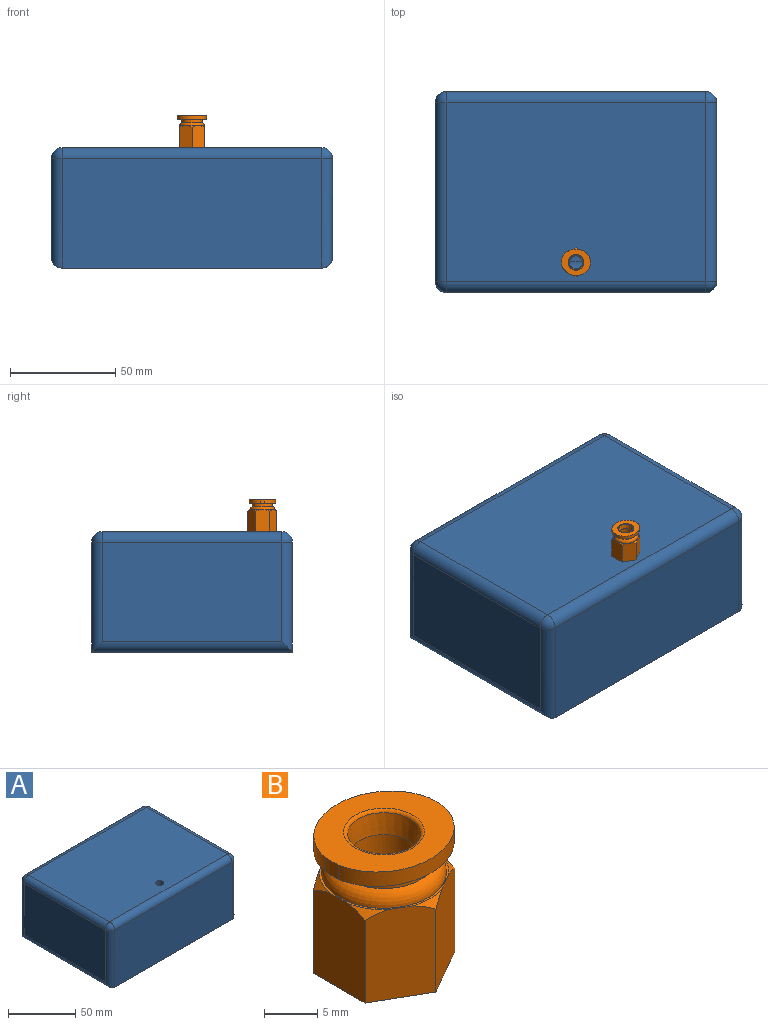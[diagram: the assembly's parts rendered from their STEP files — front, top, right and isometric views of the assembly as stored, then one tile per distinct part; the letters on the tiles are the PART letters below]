
ASSEMBLY  parts=2 mates=1
PART A: 47 faces, bbox 133.4x95.3x57.2 mm
  f0: plane 65.41x27.31mm, normal (-1,0,0), area 1785.9mm2, adj f18,f27,f28,f32
  f1: plane 103.51x27.31mm, normal (0,-1,0), area 2826.2mm2, adj f19,f20,f28,f29
  f2: plane 65.41x27.31mm, normal (1,0,0), area 1785.9mm2, adj f13,f16,f20,f21
  f3: plane 103.51x27.31mm, normal (0,1,0), area 2826.2mm2, adj f16,f17,f26,f27
  f4: plane 103.51x65.41mm, normal (0,0,-1), area 6758.9mm2, adj f6,f21,f26,f29,f32
  f5: plane 103.51x65.41mm, normal (0,0,1), area 6769.7mm2, adj f13,f17,f18,f19
  f6: cylinder r=3.11mm len=6.22mm, axis (0,0,1), area 97mm2, adj f4,f11,f26
  f7: plane 85.09x46.99mm, normal (1,0,0), area 3998.4mm2, adj f41,f43,f45,f46
  f8: plane 123.19x52.07mm, normal (0,1,0), area 6414.5mm2, adj f12,f37,f42,f46
  f9: plane 85.09x46.99mm, normal (-1,0,0), area 3998.4mm2, adj f33,f34,f36,f37
  f10: plane 123.19x52.07mm, normal (0,-1,0), area 6414.5mm2, adj f12,f33,f38,f43
  f11: plane 123.19x85.09mm, normal (0,0,1), area 10451.9mm2, adj f6,f36,f38,f41,f42
  f12: plane 123.19x95.25mm, normal (0,0,-1), area 11733.8mm2, adj f8,f10,f34,f45
  f13: cylinder r=10.16mm len=65.41mm, axis (0,1,0), area 1043.8mm2, adj f2,f5,f14,f15
  f14: sphere r=10.16mm, area 162.1mm2, adj f13,f16,f17
  f15: sphere r=10.16mm, area 162.1mm2, adj f13,f19,f20
  f16: cylinder r=10.16mm len=27.31mm, axis (0,0,1), area 435.8mm2, adj f2,f3,f14,f22
  f17: cylinder r=10.16mm len=103.51mm, axis (-1,0,0), area 1651.9mm2, adj f3,f5,f14,f23
  f18: cylinder r=10.16mm len=65.41mm, axis (0,-1,0), area 1043.8mm2, adj f0,f5,f23,f24
  f19: cylinder r=10.16mm len=103.51mm, axis (1,0,0), area 1651.9mm2, adj f1,f5,f15,f24
  f20: cylinder r=10.16mm len=27.31mm, axis (0,0,-1), area 435.8mm2, adj f1,f2,f15,f25
  f21: cylinder r=10.16mm len=65.41mm, axis (0,-1,0), area 1043.8mm2, adj f2,f4,f22,f25
  f22: sphere r=10.16mm, area 162.1mm2, adj f16,f21,f26
  f23: sphere r=10.16mm, area 162.1mm2, adj f17,f18,f27
  f24: sphere r=10.16mm, area 162.1mm2, adj f18,f19,f28
  f25: sphere r=10.16mm, area 162.1mm2, adj f20,f21,f29
  f26: cylinder r=10.16mm len=103.51mm, axis (1,0,0), area 1632mm2, adj f3,f4,f6,f22,f30
  f27: cylinder r=10.16mm len=27.31mm, axis (0,0,-1), area 435.8mm2, adj f0,f3,f23,f30
  f28: cylinder r=10.16mm len=27.31mm, axis (0,0,1), area 435.8mm2, adj f0,f1,f24,f31
  f29: cylinder r=10.16mm len=103.51mm, axis (-1,0,0), area 1651.9mm2, adj f1,f4,f25,f31
  f30: sphere r=10.16mm, area 162.1mm2, adj f26,f27,f32
  f31: sphere r=10.16mm, area 162.1mm2, adj f28,f29,f32
  f32: cylinder r=10.16mm len=65.41mm, axis (0,1,0), area 1043.8mm2, adj f0,f4,f30,f31
  f33: cylinder r=5.08mm len=52.07mm, axis (0,0,-1), area 400.8mm2, adj f9,f10,f34,f35
  f34: cylinder r=5.08mm len=95.25mm, axis (0,-1,0), area 730.6mm2, adj f9,f12,f33,f37
  f35: sphere r=5.08mm, area 40.5mm2, adj f33,f36,f38
  f36: cylinder r=5.08mm len=85.09mm, axis (0,1,0), area 679mm2, adj f9,f11,f35,f39
  f37: cylinder r=5.08mm len=52.07mm, axis (0,0,1), area 400.8mm2, adj f8,f9,f34,f39
  f38: cylinder r=5.08mm len=123.19mm, axis (-1,0,0), area 983mm2, adj f10,f11,f35,f40
  f39: sphere r=5.08mm, area 40.5mm2, adj f36,f37,f42
  f40: sphere r=5.08mm, area 40.5mm2, adj f38,f41,f43
  f41: cylinder r=5.08mm len=85.09mm, axis (0,-1,0), area 679mm2, adj f7,f11,f40,f44
  f42: cylinder r=5.08mm len=123.19mm, axis (1,0,0), area 983mm2, adj f8,f11,f39,f44
  f43: cylinder r=5.08mm len=52.07mm, axis (0,0,1), area 400.8mm2, adj f7,f10,f40,f45
  f44: sphere r=5.08mm, area 40.5mm2, adj f41,f42,f46
  f45: cylinder r=5.08mm len=95.25mm, axis (0,1,0), area 730.6mm2, adj f7,f12,f43,f46
  f46: cylinder r=5.08mm len=52.07mm, axis (0,0,-1), area 400.8mm2, adj f7,f8,f44,f45
PART B: 26 faces, bbox 14.1x14x15.3 mm
  f0: plane 10.58x7.14mm, normal (1,0,0), area 69.2mm2, adj f1,f5,f7,f19,f20,f23
  f1: plane 10.57x6.22mm, normal (0.5,0.87,0), area 69.2mm2, adj f0,f2,f7,f15,f20,f23
  f2: plane 10.57x6.22mm, normal (-0.5,0.87,0), area 69.2mm2, adj f1,f3,f7,f15,f16,f23
  f3: plane 10.58x7.14mm, normal (-1,0,0), area 69.2mm2, adj f2,f4,f7,f16,f17,f23
  f4: plane 10.57x6.22mm, normal (-0.5,-0.87,0), area 69.2mm2, adj f3,f5,f7,f17,f18,f23
  f5: plane 10.57x6.22mm, normal (0.5,-0.87,0), area 69.2mm2, adj f0,f4,f7,f18,f19,f23
  f6: cylinder r=6.9mm len=1.74mm, axis (0,0,1), area 2.9mm2, adj f12,f14,f21,f22
  f7: plane 12.14x11.89mm, normal (0,0,1), area 7.3mm2, adj f0,f1,f2,f3,f4,f5,f8,f15
  f8: cylinder r=5.84mm len=11.68mm, axis (0,0,1), area 0.3mm2, adj f7,f10
  f9: torus R=3.79mm, axis (0,0,1), area 10.8mm2, adj f14,f25
  f10: torus R=4.25mm, axis (0,0,1), area 67.8mm2, adj f8,f11
  f11: cylinder r=4.76mm len=9.53mm, axis (0,0,1), area 45.6mm2, adj f10,f12
  f12: plane 13.79x12.45mm, normal (0,0,-1), area 63.8mm2, adj f6,f11,f13,f21,f22
  f13: cylinder r=6.9mm len=1.74mm, axis (0,0,1), area 2.9mm2, adj f12,f14,f21,f22
  f14: plane 13.79x12.45mm, normal (0,0,1), area 90mm2, adj f6,f9,f13,f21,f22
  f15: cone r=6.86mm half-angle=45deg, axis (0,0,-1), area 2.3mm2, adj f1,f2,f7
  f16: cone r=6.86mm half-angle=45deg, axis (0,0,-1), area 2.3mm2, adj f2,f3,f7
  f17: cone r=6.86mm half-angle=45deg, axis (0,0,-1), area 2.3mm2, adj f3,f4,f7
  f18: cone r=6.86mm half-angle=45deg, axis (0,0,-1), area 2.3mm2, adj f4,f5,f7
  f19: cone r=6.86mm half-angle=45deg, axis (0,0,-1), area 2.3mm2, adj f0,f5,f7
  f20: cone r=6.86mm half-angle=45deg, axis (0,0,-1), area 2.3mm2, adj f0,f1,f7
  f21: extruded ~13.68x5.35mm, area 31.2mm2, adj f6,f12,f13,f14
  f22: extruded ~13.68x5.35mm, area 31.2mm2, adj f6,f12,f13,f14
  f23: plane 13.73x11.89mm, normal (0,0,-1), area 92mm2, adj f0,f1,f2,f3,f4,f5,f24
  f24: cylinder r=3.11mm len=12.44mm, axis (0,0,-1), area 243.1mm2, adj f23,f25
  f25: cone r=3.06mm half-angle=7.6deg, axis (0,0,1), area 47.2mm2, adj f9,f24
PLACE A t=(54.49,47.49,20.88)mm
PLACE B t=(54.49,14.09,82.35)mm
MATE fastened B.f24 <-> A.f6  axis (0,0,-1) through (54.49,14.09,78.03)mm
